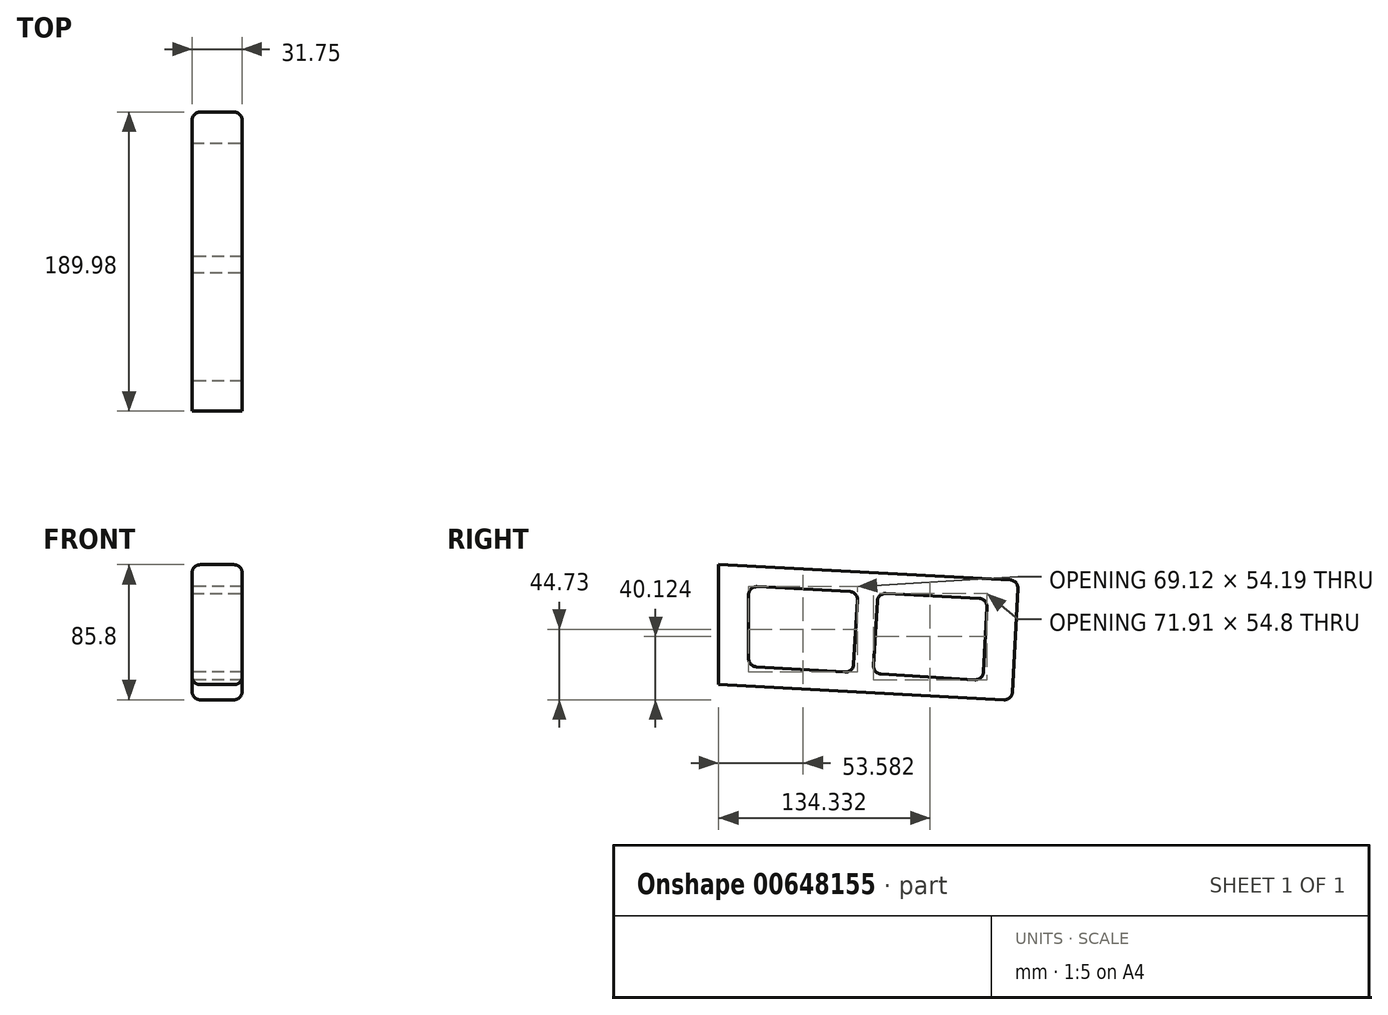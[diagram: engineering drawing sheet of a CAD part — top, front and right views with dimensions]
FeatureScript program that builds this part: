
annotation { "Feature Type Name" : "Feature", "Feature Type Description" : "" }
export const myFeature = defineFeature(function(context is Context, id is Id, definition is map)
    precondition{}
    {
        {
            var Q0;
            Q0=qCreatedBy(makeId("Right.planeOp"),FACE);
            var sketch = newSketch(context, id + "F0", { "sketchPlane" : qUnion([Q0])});
            skLineSegment(sketch, "E0.right", {"start": v(0, 0) * mm, "end": v(0, 76.2) * mm});
            skLineSegment(sketch, "E1", {"start": v(0, 76.2) * mm, "end": v(190.24, 66.23) * mm});
            skLineSegment(sketch, "E2", {"start": v(190.24, 66.23) * mm, "end": v(186.25, -9.87) * mm});
            skLineSegment(sketch, "E3", {"start": v(0, 0) * mm, "end": v(186.25, -9.87) * mm});
            skLineSegment(sketch, "E4", {"start": v(0, 0) * mm, "end": v(19.02, -1) * mm});
            skLineSegment(sketch, "E5", {"start": v(19.02, 62.5) * mm, "end": v(19.02, 11.7) * mm});
            skLineSegment(sketch, "E6", {"start": v(170.55, 54.54) * mm, "end": v(167.87, 2.82) * mm});
            skLineSegment(sketch, "E7", {"start": v(98.07, 6.98) * mm, "end": v(101.13, 58.2) * mm});
            skLineSegment(sketch, "E8", {"start": v(88.45, 58.86) * mm, "end": v(85.4, 7.73) * mm});
            skLineSegment(sketch, "E9", {"start": v(19.02, 11.7) * mm, "end": v(85.4, 7.73) * mm});
            skLineSegment(sketch, "E10", {"start": v(98.07, 6.98) * mm, "end": v(167.87, 2.82) * mm});
            skLineSegment(sketch, "E11", {"start": v(19.02, 62.5) * mm, "end": v(88.45, 58.86) * mm});
            skLineSegment(sketch, "E12", {"start": v(101.13, 58.2) * mm, "end": v(170.55, 54.54) * mm});
            skLineSegment(sketch, "E13", {"start": v(0, 76.2) * mm, "end": v(0, 44.45) * mm});
            skLineSegment(sketch, "E14", {"start": v(0, 76.2) * mm, "end": v(0, 69.85) * mm});
            skLineSegment(sketch, "E15", {"start": v(0, 44.45) * mm, "end": v(0, 50.8) * mm});
            skSolve(sketch);
        }
        {
            var Q0;
            Q0=makeQuery(id+"F0.imprint","IMPRINT",FACE,{"disambiguationData":[TD([[makeQuery(id+"F0.imprint","IMPRINT",EDGE,{"derivedFrom":sQuery(id+"F0.wireOp",EDGE,"E0.right")}),-1.0]])]});
            extrude(context, id + "F1", {"entities" : qUnion([Q0]), "depth" : 31.75 * mm, "offsetDistance" : 25.4 * mm});
        }
        {
            var Q0;
            Q0=makeQuery(id+"F1.opExtrude","CAP_EDGE",EDGE,{"disambiguationData":[OSD([sQuery(id+"F0.wireOp",EDGE,"E2")])],"isStart":false});
            var Q1;
            Q1=makeQuery(id+"F1.opExtrude","CAP_EDGE",EDGE,{"disambiguationData":[OSD([sQuery(id+"F0.wireOp",EDGE,"E2")])],"isStart":true});
            var Q2;
            Q2=makeQuery(id+"F1.opExtrude","SWEPT_EDGE",EDGE,{"disambiguationData":[OSD([sQuery(id+"F0.wireOp",EDGE,"E1"),sQuery(id+"F0.wireOp",EDGE,"E2")])]});
            var Q3;
            Q3=makeQuery(id+"F1.opExtrude","SWEPT_EDGE",EDGE,{"disambiguationData":[OSD([sQuery(id+"F0.wireOp",EDGE,"E2"),sQuery(id+"F0.wireOp",EDGE,"E3")])]});
            var Q4;
            Q4=makeQuery(id+"F1.opExtrude","CAP_EDGE",EDGE,{"disambiguationData":[OSD([sQuery(id+"F0.wireOp",EDGE,"E3"),sQuery(id+"F0.wireOp",EDGE,"E4")])],"isStart":false});
            var Q5;
            Q5=makeQuery(id+"F1.opExtrude","CAP_EDGE",EDGE,{"disambiguationData":[OSD([sQuery(id+"F0.wireOp",EDGE,"E1")])],"isStart":false});
            var Q6;
            Q6=makeQuery(id+"F1.opExtrude","CAP_EDGE",EDGE,{"disambiguationData":[OSD([sQuery(id+"F0.wireOp",EDGE,"E1")])],"isStart":true});
            var Q7;
            Q7=makeQuery(id+"F1.opExtrude","CAP_EDGE",EDGE,{"disambiguationData":[OSD([sQuery(id+"F0.wireOp",EDGE,"E3"),sQuery(id+"F0.wireOp",EDGE,"E4")])],"isStart":true});
            var Q8;
            Q8=makeQuery(id+"F1.opExtrude","SWEPT_EDGE",EDGE,{"disambiguationData":[OSD([sQuery(id+"F0.wireOp",EDGE,"E6"),sQuery(id+"F0.wireOp",EDGE,"E10")])]});
            var Q9;
            Q9=makeQuery(id+"F1.opExtrude","SWEPT_EDGE",EDGE,{"disambiguationData":[OSD([sQuery(id+"F0.wireOp",EDGE,"E6"),sQuery(id+"F0.wireOp",EDGE,"E12")])]});
            var Q10;
            Q10=makeQuery(id+"F1.opExtrude","SWEPT_EDGE",EDGE,{"disambiguationData":[OSD([sQuery(id+"F0.wireOp",EDGE,"E7"),sQuery(id+"F0.wireOp",EDGE,"E12")])]});
            var Q11;
            Q11=makeQuery(id+"F1.opExtrude","SWEPT_EDGE",EDGE,{"disambiguationData":[OSD([sQuery(id+"F0.wireOp",EDGE,"E7"),sQuery(id+"F0.wireOp",EDGE,"E10")])]});
            var Q12;
            Q12=makeQuery(id+"F1.opExtrude","SWEPT_EDGE",EDGE,{"disambiguationData":[OSD([sQuery(id+"F0.wireOp",EDGE,"E8"),sQuery(id+"F0.wireOp",EDGE,"E11")])]});
            var Q13;
            Q13=makeQuery(id+"F1.opExtrude","SWEPT_EDGE",EDGE,{"disambiguationData":[OSD([sQuery(id+"F0.wireOp",EDGE,"E8"),sQuery(id+"F0.wireOp",EDGE,"E9")])]});
            var Q14;
            Q14=makeQuery(id+"F1.opExtrude","SWEPT_EDGE",EDGE,{"disambiguationData":[OSD([sQuery(id+"F0.wireOp",EDGE,"E5"),sQuery(id+"F0.wireOp",EDGE,"E9")])]});
            var Q15;
            Q15=makeQuery(id+"F1.opExtrude","SWEPT_EDGE",EDGE,{"disambiguationData":[OSD([sQuery(id+"F0.wireOp",EDGE,"E5"),sQuery(id+"F0.wireOp",EDGE,"E11")])]});
            fillet(context, id + "F2", {"entities" : qUnion([Q0, Q1, Q2, Q3, Q4, Q5, Q6, Q7, Q8, Q9, Q10, Q11, Q12, Q13, Q14, Q15]), "radius" : 5.08 * mm, "tangentPropagation" : true, "allowEdgeOverflow" : false});
        }
    });
